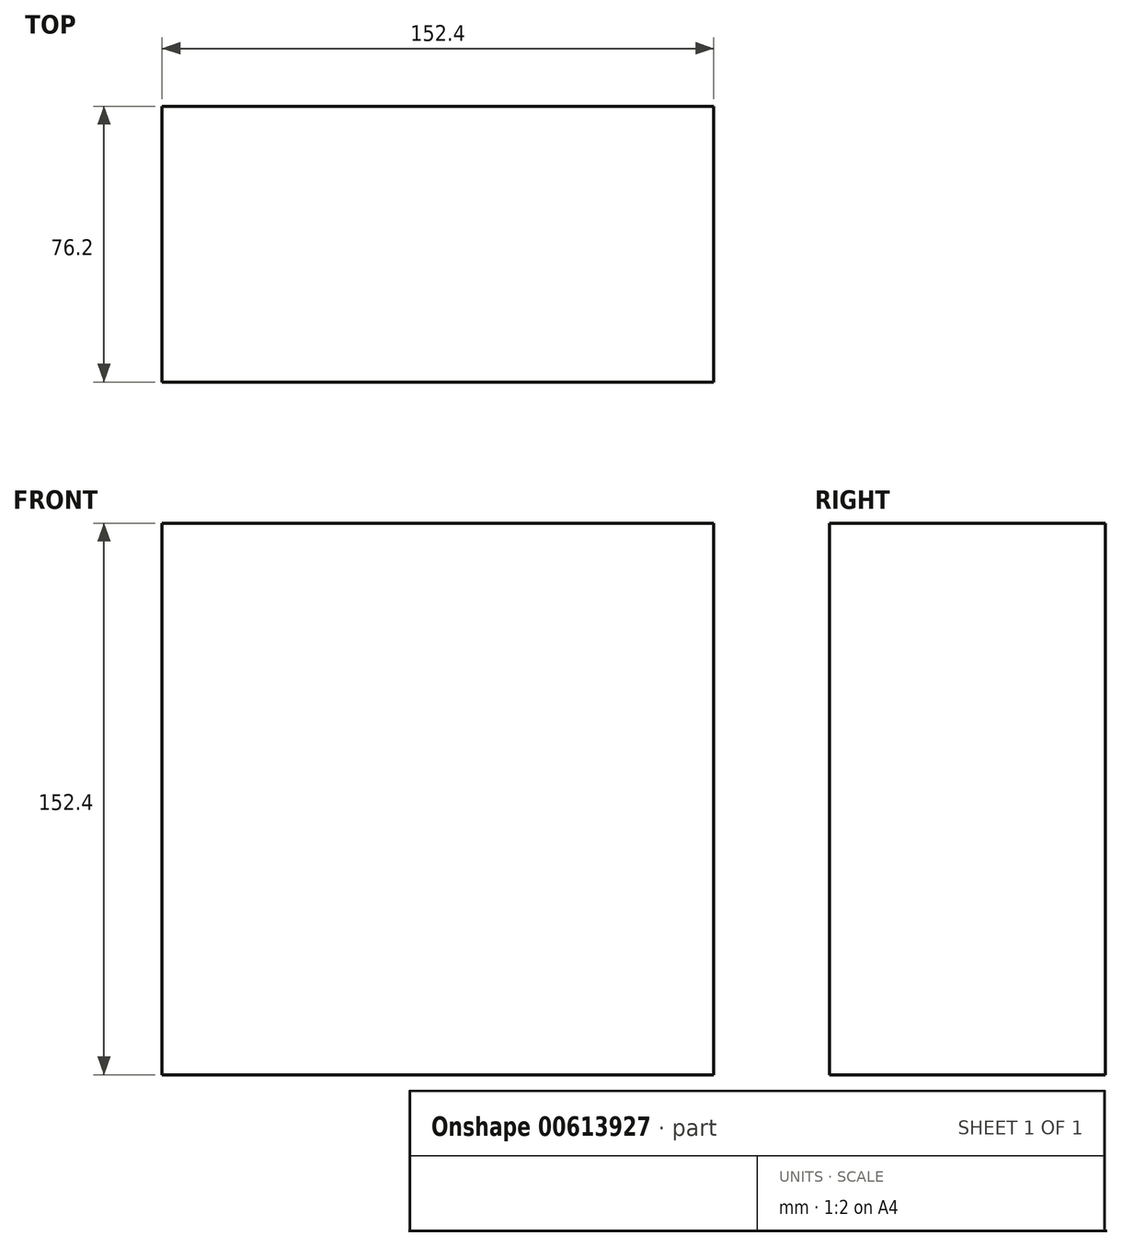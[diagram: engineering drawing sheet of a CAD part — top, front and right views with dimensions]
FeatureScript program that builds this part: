
annotation { "Feature Type Name" : "Feature", "Feature Type Description" : "" }
export const myFeature = defineFeature(function(context is Context, id is Id, definition is map)
    precondition{}
    {
        {
            var Q0;
            Q0=qCreatedBy(makeId("Top.planeOp"),FACE);
            var sketch = newSketch(context, id + "F0", { "sketchPlane" : qUnion([Q0])});
            skLineSegment(sketch, "E0.bottom", {"start": v(-64.98, 13.15) * mm, "end": v(87.42, 13.15) * mm});
            skLineSegment(sketch, "E0.top", {"start": v(-64.98, -63.05) * mm, "end": v(87.42, -63.05) * mm});
            skLineSegment(sketch, "E0.left", {"start": v(-64.98, 13.15) * mm, "end": v(-64.98, -63.05) * mm});
            skLineSegment(sketch, "E0.right", {"start": v(87.42, 13.15) * mm, "end": v(87.42, -63.05) * mm});
            skSolve(sketch);
        }
        {
            var Q0;
            Q0 = qSketchRegion(id + "F0", true);
            extrude(context, id + "F1", {"entities" : qUnion([Q0]), "depth" : 152.4 * mm, "offsetDistance" : 25.4 * mm});
        }
    });
